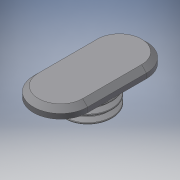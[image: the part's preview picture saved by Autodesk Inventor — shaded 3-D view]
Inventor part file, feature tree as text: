
AUTODESK INVENTOR PART (.ipt)
format: ipt  version: 2016 SP2 (Build 200236200, 236)  size: 415,232 bytes
history: native  units: mm
features: sketch x5, extrude x2, revolve x2, thread x1, other x1, chamfer x1
ambient origin geometry x8: Origin, YZ Plane, XZ Plane, XY Plane, X Axis, Y Axis, Z Axis, Center Point
bodies: Volumenkörper1 (feature_tree), Volumenkörper2 (feature_tree)
feature tree (12):
  extrude  "Extrusion1"  Depth=5.0mm TaperAngle=0.0deg
  thread  "Gewinde1"  [1 undecoded]
  revolve  "Umdrehung1"
  revolve  "Umdrehung2"
  other  "Spirale1"
  extrude  "Extrusion2"  Depth=1.5mm
  chamfer  "Fase1"  Distance=6.0mm
  sketch  "Skizze1"  dims[d0=9.5mm d1=5.0mm d2=0.0mm d3=10.0mm d4=0.0mm]
  sketch  "Skizze2"  dims[d5=60.0deg d6=0.240125mm d7=0.240125mm d10=1.5mm]
  sketch  "Skizze3"  dims[d12=60.0deg]
  sketch  "Skizze4"  dims[d14=0.0mm]
  sketch  "Skizze5"  dims[d15=0.0mm d16=1.5015mm d17=8.0mm d18=10.0mm d19=0.0mm d20=0.0mm d21=0.0mm d22=0.0mm d23=0.0mm d24=6.0mm d25=5.5mm d26=2.0mm d27=0.0mm d28=1.0mm d29=2.0mm d30=45.0deg]
note: 1 required parameter value undecoded (feature->parameter linkage not recoverable at this tier; creation-order binding heuristic only, values carry confidence <= 0.55)
